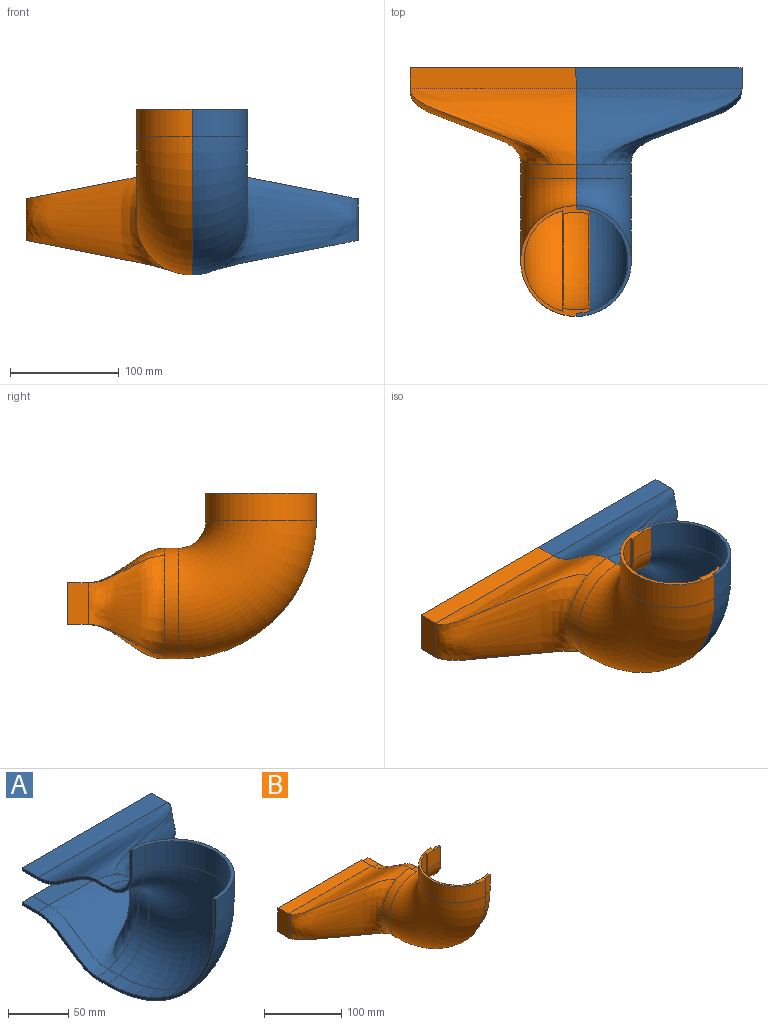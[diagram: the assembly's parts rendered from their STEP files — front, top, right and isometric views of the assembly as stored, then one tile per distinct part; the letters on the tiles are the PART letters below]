
ASSEMBLY  parts=2 mates=1
PART A: 32 faces, bbox 212.2x245.1x168.9 mm
  f0: offset ~133x93.99mm, area 7690.1mm2, adj f1,f2,f4,f6
  f1: offset ~172.12x75.85mm, area 5473.3mm2, adj f0,f2,f5,f29
  f2: cylinder r=47.8mm len=92.16mm, axis (0,-1,0), area 1580.6mm2, adj f0,f1,f3,f4,f12,f25
  f3: torus R=76.2mm, axis (-1,0,0), area 14897.1mm2, adj f2,f9,f11,f13
  f4: offset ~172.12x75.85mm, area 5473.7mm2, adj f0,f2,f7,f14
  f5: plane 136.7x19.05mm, normal (0,0,-1), area 2604.1mm2, adj f1,f6,f23,f28
  f6: plane 32.1x19.05mm, normal (-1,0,0), area 611.5mm2, adj f0,f5,f7,f23
  f7: plane 136.7x19.05mm, normal (0,0,1), area 2604.1mm2, adj f4,f6,f23,f24
  f8: plane 38.1x19.05mm, normal (1,0,0), area 725.8mm2, adj f10,f21,f22,f23
  f9: cylinder r=47.8mm len=92.16mm, axis (0,0,1), area 3161.3mm2, adj f3,f20,f26,f27
  f10: bspline ~127x87.99mm, area 8559.2mm2, adj f8,f15,f16,f19
  f11: torus R=76.2mm, axis (-1,0,0), area 585mm2, adj f3,f12,f27,f30
  f12: cylinder r=47.8mm len=12.7mm, axis (0,-1,0), area 163.3mm2, adj f2,f11,f29,f30
  f13: torus R=76.2mm, axis (-1,0,0), area 2492.2mm2, adj f3,f25,f26,f31
  f14: offset ~158.4x75.85mm, area 990.5mm2, adj f4,f24,f25,f31
  f15: bspline ~206.25x69.85mm, area 6770.8mm2, adj f10,f19,f22,f30
  f16: bspline ~206.25x69.85mm, area 6770.8mm2, adj f10,f19,f21,f31
  f17: cylinder r=50.8mm len=101.6mm, axis (0,0,1), area 4053.7mm2, adj f18,f20,f30,f31
  f18: torus R=76.2mm, axis (-1,0,0), area 19102.4mm2, adj f17,f19,f30,f31
  f19: cylinder r=50.8mm len=101.6mm, axis (0,-1,0), area 2026.8mm2, adj f10,f15,f16,f18,f30,f31
  f20: plane 101.6x50.8mm, normal (0,0,1), area 464.6mm2, adj f9,f17,f26,f27,f30,f31
  f21: plane 152.4x19.05mm, normal (0,0,-1), area 2903.2mm2, adj f8,f16,f23,f31
  f22: plane 152.4x19.05mm, normal (0,0,1), area 2903.2mm2, adj f8,f15,f23,f30
  f23: plane 152.4x38.1mm, normal (0,1,0), area 1010.7mm2, adj f5,f6,f7,f8,f21,f22,f24,f28
  f24: plane 19.05x12.7mm, normal (0,0,1), area 241.9mm2, adj f7,f14,f23,f31
  f25: cylinder r=47.8mm len=12.7mm, axis (0,-1,0), area 163.3mm2, adj f2,f13,f14,f31
  f26: cylinder r=47.8mm len=25.4mm, axis (0,0,1), area 326.5mm2, adj f9,f13,f20,f31
  f27: cylinder r=47.8mm len=25.4mm, axis (0,0,1), area 326.5mm2, adj f9,f11,f20,f30
  f28: plane 19.05x12.7mm, normal (0,0,-1), area 241.9mm2, adj f5,f23,f29,f30
  f29: offset ~158.4x75.85mm, area 990.5mm2, adj f1,f12,f28,f30
  f30: plane 130.91x86.46mm, normal (-1,0,0), area 532.5mm2, adj f11,f12,f15,f17,f18,f19,f20,f22
  f31: plane 229.55x153.35mm, normal (-1,0,0), area 997.1mm2, adj f13,f14,f16,f17,f18,f19,f20,f21
PART B: 62 faces, bbox 269x251.1x174.9 mm
  f0: plane 12.7x2.89mm, normal (0.96,0,0.27), area 38.1mm2, adj f1,f11,f13,f18
  f1: bspline ~69.85x33.03mm, area 232.7mm2, adj f0,f2,f14,f19
  f2: plane 19.05x3mm, normal (1,0,0), area 57.1mm2, adj f1,f3,f15,f20
  f3: plane 165.1x38.1mm, normal (0,1,0), area 1163.1mm2, adj f2,f4,f15,f20,f26,f27,f36,f41
  f4: plane 19.05x3mm, normal (-1,0,0), area 57.1mm2, adj f3,f5,f15,f54
  f5: bspline ~69.85x33.03mm, area 232.7mm2, adj f4,f6,f14,f49
  f6: plane 12.7x2.89mm, normal (-0.96,0,0.27), area 38.1mm2, adj f5,f7,f13,f53
  f7: cone r=122.28mm half-angle=74.6deg, axis (-1,0,0), area 569.4mm2, adj f6,f8,f16,f55
  f8: plane 25.4x2.89mm, normal (-0.96,0.27,0), area 76.2mm2, adj f7,f9,f12,f50
  f9: plane 101.6x63.5mm, normal (0,0,1), area 614.1mm2, adj f8,f10,f12,f17,f22,f31,f32,f37
  f10: plane 25.4x2.89mm, normal (0.96,0.27,0), area 76.2mm2, adj f9,f11,f12,f17
  f11: cone r=122.28mm half-angle=74.6deg, axis (1,0,0), area 569.4mm2, adj f0,f10,f16,f21
  f12: cylinder r=44.8mm len=25.4mm, axis (0,0,1), area 612mm2, adj f8,f9,f10,f16
  f13: cylinder r=44.8mm len=23.81mm, axis (0,-1,0), area 306mm2, adj f0,f6,f14,f16
  f14: offset ~215.2x81.85mm, area 1957.8mm2, adj f1,f5,f13,f15
  f15: plane 25.4x19.05mm, normal (0,0,1), area 483.9mm2, adj f2,f3,f4,f14
  f16: torus R=76.2mm, axis (-1,0,0), area 4559.3mm2, adj f7,f11,f12,f13
  f17: cylinder r=47.8mm len=25.4mm, axis (0,0,1), area 326.5mm2, adj f9,f10,f21,f61
  f18: cylinder r=47.8mm len=12.7mm, axis (0,-1,0), area 163.3mm2, adj f0,f19,f21,f61
  f19: offset ~158.4x75.85mm, area 990.6mm2, adj f1,f18,f20,f61
  f20: plane 19.05x12.7mm, normal (0,0,-1), area 241.9mm2, adj f2,f3,f19,f61
  f21: torus R=76.2mm, axis (-1,0,0), area 2492.2mm2, adj f11,f17,f18,f61
  f22: plane 25.4x2.89mm, normal (-0.96,-0.27,0), area 76.2mm2, adj f9,f23,f32,f50
  f23: cone r=30.12mm half-angle=74.6deg, axis (1,0,0), area 148.7mm2, adj f22,f24,f33,f55
  f24: plane 12.7x2.89mm, normal (-0.96,0,-0.27), area 38.1mm2, adj f23,f25,f34,f53
  f25: bspline ~69.85x33.03mm, area 232.7mm2, adj f24,f26,f35,f52
  f26: plane 19.05x3mm, normal (-1,0,0), area 57.1mm2, adj f3,f25,f36,f51
  f27: plane 19.05x3mm, normal (1,0,0), area 57.1mm2, adj f3,f28,f36,f41
  f28: bspline ~69.85x33.03mm, area 232.7mm2, adj f27,f29,f35,f40
  f29: plane 12.7x2.89mm, normal (0.96,0,-0.27), area 38.1mm2, adj f28,f30,f34,f39
  f30: cone r=30.12mm half-angle=74.6deg, axis (-1,0,0), area 148.7mm2, adj f29,f31,f33,f38
  f31: plane 25.4x2.89mm, normal (0.96,-0.27,0), area 76.2mm2, adj f9,f30,f32,f37
  f32: cylinder r=44.8mm len=25.4mm, axis (0,0,1), area 612mm2, adj f9,f22,f31,f33
  f33: torus R=76.2mm, axis (-1,0,0), area 1208.8mm2, adj f23,f30,f32,f34
  f34: cylinder r=44.8mm len=23.81mm, axis (0,-1,0), area 306mm2, adj f24,f29,f33,f35
  f35: offset ~215.2x81.85mm, area 1966.8mm2, adj f25,f28,f34,f36
  f36: plane 25.4x19.05mm, normal (0,0,-1), area 483.9mm2, adj f3,f26,f27,f35
  f37: cylinder r=47.8mm len=25.4mm, axis (0,0,1), area 326.5mm2, adj f9,f31,f38,f60
  f38: torus R=76.2mm, axis (-1,0,0), area 585mm2, adj f30,f37,f39,f60
  f39: cylinder r=47.8mm len=12.7mm, axis (0,-1,0), area 163.3mm2, adj f29,f38,f40,f60
  f40: offset ~158.4x75.85mm, area 987.5mm2, adj f28,f39,f41,f60
  f41: plane 19.05x12.7mm, normal (0,0,1), area 241.9mm2, adj f3,f27,f40,f60
  f42: plane 152.4x19.05mm, normal (0,0,1), area 2903.2mm2, adj f3,f48,f56,f60
  f43: plane 152.4x19.05mm, normal (0,0,-1), area 2903.2mm2, adj f3,f47,f56,f61
  f44: cylinder r=50.8mm len=101.6mm, axis (0,-1,0), area 2026.8mm2, adj f45,f47,f48,f58,f60,f61
  f45: torus R=76.2mm, axis (-1,0,0), area 19102.4mm2, adj f44,f46,f60,f61
  f46: cylinder r=50.8mm len=101.6mm, axis (0,0,1), area 4053.7mm2, adj f9,f45,f60,f61
  f47: bspline ~161.8x69.85mm, area 6770.8mm2, adj f43,f44,f58,f61
  f48: bspline ~206.25x69.85mm, area 6770.8mm2, adj f42,f44,f58,f60
  f49: offset ~165.77x75.85mm, area 5473.3mm2, adj f5,f53,f54,f59
  f50: cylinder r=47.8mm len=92.16mm, axis (0,0,1), area 3161.3mm2, adj f8,f9,f22,f55
  f51: plane 136.7x19.05mm, normal (0,0,-1), area 2604.1mm2, adj f3,f26,f52,f57
  f52: offset ~172.12x75.85mm, area 5473.7mm2, adj f25,f51,f53,f59
  f53: cylinder r=47.8mm len=92.16mm, axis (0,-1,0), area 1580.6mm2, adj f6,f24,f49,f52,f55,f59
  f54: plane 136.7x19.05mm, normal (0,0,1), area 2604.1mm2, adj f3,f4,f49,f57
  f55: torus R=76.2mm, axis (-1,0,0), area 14897.1mm2, adj f7,f23,f50,f53
  f56: plane 38.1x19.05mm, normal (-1,0,0), area 725.8mm2, adj f3,f42,f43,f58
  f57: plane 32.1x19.05mm, normal (1,0,0), area 611.5mm2, adj f3,f51,f54,f59
  f58: bspline ~127x87.99mm, area 8559.2mm2, adj f44,f47,f48,f56
  f59: offset ~133x93.99mm, area 7690.3mm2, adj f49,f52,f53,f57
  f60: plane 134.32x89.87mm, normal (1,0,0), area 532.5mm2, adj f3,f9,f37,f38,f39,f40,f41,f42
  f61: plane 232.89x156.69mm, normal (1,0,0), area 997.1mm2, adj f3,f9,f17,f18,f19,f20,f21,f43
PLACE A t=(-196.92,20.06,-82.49)mm
PLACE B t=(-196.92,20.06,-82.49)mm
MATE fastened A.f30 <-> B.f60  axis (-1,0,0) through (-196.92,39.11,-63.44)mm
